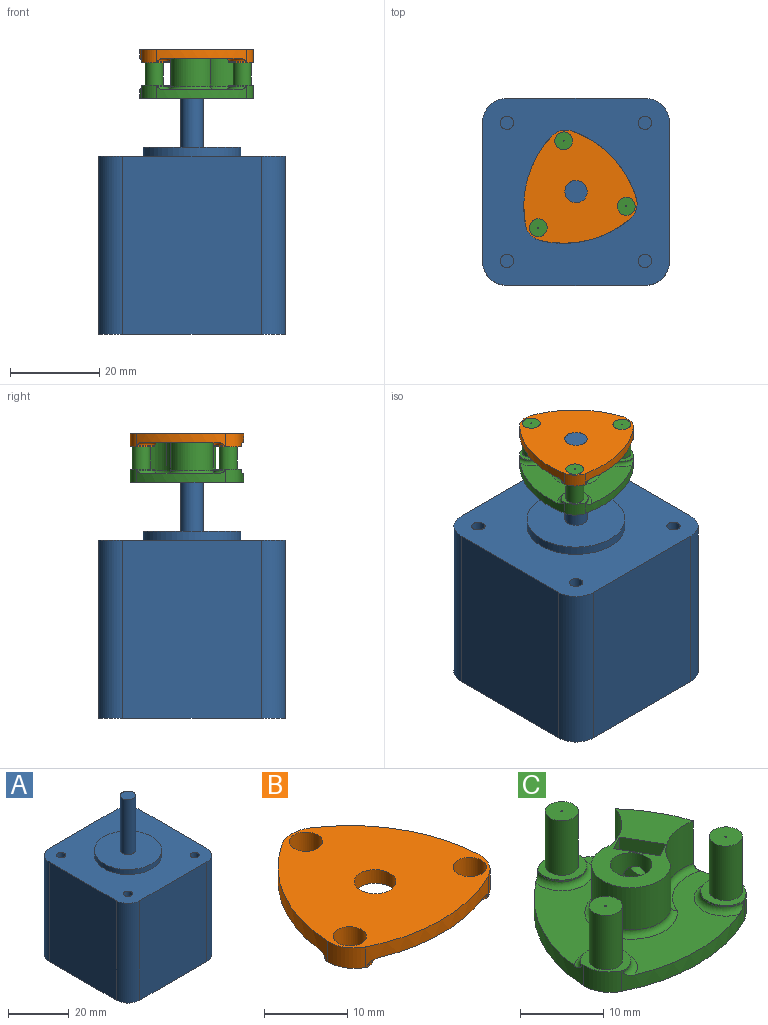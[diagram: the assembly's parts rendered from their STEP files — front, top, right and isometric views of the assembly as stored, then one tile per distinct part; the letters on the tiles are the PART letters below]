
ASSEMBLY  parts=3 mates=2
PART A: 22 faces, bbox 42x42x64 mm
  f0: plane 42x42mm, normal (0,0,1), area 1329.6mm2, adj f1,f2,f3,f4,f5,f6,f7,f8
  f1: plane 40x31mm, normal (1,0,0), area 1240mm2, adj f0,f2,f8,f9
  f2: cylinder r=5.5mm len=40mm, axis (0,0,1), area 345.6mm2, adj f0,f1,f3,f9
  f3: plane 40x31mm, normal (0,1,0), area 1240mm2, adj f0,f2,f4,f9
  f4: cylinder r=5.5mm len=40mm, axis (0,0,1), area 345.6mm2, adj f0,f3,f5,f9
  f5: plane 40x31mm, normal (-1,0,0), area 1240mm2, adj f0,f4,f6,f9
  f6: cylinder r=5.5mm len=40mm, axis (0,0,1), area 345.6mm2, adj f0,f5,f7,f9
  f7: plane 40x31mm, normal (0,-1,0), area 1240mm2, adj f0,f6,f8,f9
  f8: cylinder r=5.5mm len=40mm, axis (0,0,1), area 345.6mm2, adj f0,f1,f7,f9
  f9: plane 42x42mm, normal (0,0,-1), area 1738mm2, adj f1,f2,f3,f4,f5,f6,f7,f8
  f10: cylinder r=11mm len=22mm, axis (0,0,-1), area 138.2mm2, adj f0,f11
  f11: plane 22x22mm, normal (0,0,1), area 360.5mm2, adj f10,f13
  f12: plane 5x5mm, normal (0,0,1), area 19.6mm2, adj f13
  f13: cylinder r=2.5mm len=22mm, axis (0,0,-1), area 345.6mm2, adj f11,f12
  f14: cylinder r=1.5mm len=10mm, axis (0,0,1), area 94.2mm2, adj f0,f15
  f15: plane 3x3mm, normal (0,0,1), area 7.1mm2, adj f14
  f16: cylinder r=1.5mm len=10mm, axis (0,0,1), area 94.2mm2, adj f0,f17
  f17: plane 3x3mm, normal (0,0,1), area 7.1mm2, adj f16
  f18: cylinder r=1.5mm len=10mm, axis (0,0,1), area 94.2mm2, adj f0,f19
  f19: plane 3x3mm, normal (0,0,1), area 7.1mm2, adj f18
  f20: cylinder r=1.5mm len=10mm, axis (0,0,1), area 94.2mm2, adj f0,f21
  f21: plane 3x3mm, normal (0,0,1), area 7.1mm2, adj f20
PART B: 23 faces, bbox 28.5x25.4x3.4 mm
  f0: cylinder r=23mm len=8.94mm, axis (0,0,1), area 19.1mm2, adj f1,f6,f7,f16,f17,f19,f21
  f1: plane 2.6x2mm, normal (0.87,0.5,0), area 6mm2, adj f0,f2,f6,f7
  f2: cylinder r=23mm len=6.57mm, axis (0,0,1), area 19.1mm2, adj f1,f6,f7,f8,f9,f11,f20
  f3: cylinder r=23mm len=18.04mm, axis (0,0,1), area 44.3mm2, adj f6,f7,f8,f9,f11,f12,f13,f15
  f4: cylinder r=23mm len=20.83mm, axis (0,0,1), area 44.3mm2, adj f6,f7,f12,f13,f15,f16,f17,f19
  f5: cylinder r=2.5mm len=5mm, axis (0,0,1), area 31.4mm2, adj f6,f7
  f6: plane 25.28x23.69mm, normal (0,0,-1), area 353.1mm2, adj f0,f1,f2,f3,f4,f5,f20,f21
  f7: plane 25.59x25.35mm, normal (0,0,1), area 423.5mm2, adj f0,f1,f2,f3,f4,f5,f9,f10
  f8: cylinder r=3mm len=6mm, axis (0,0,1), area 2.5mm2, adj f2,f3,f11,f20
  f9: cylinder r=4.35mm len=4.75mm, axis (0,0,1), area 15.1mm2, adj f2,f3,f7,f11
  f10: cylinder r=2mm len=4mm, axis (0,0,1), area 37.7mm2, adj f7,f11
  f11: plane 6x5.35mm, normal (0,0,-1), area 13.2mm2, adj f2,f3,f8,f9,f10
  f12: cylinder r=3mm len=6mm, axis (0,0,1), area 2.5mm2, adj f3,f4,f15,f22
  f13: cylinder r=4.35mm len=4.12mm, axis (0,0,1), area 15.1mm2, adj f3,f4,f7,f15
  f14: cylinder r=2mm len=4mm, axis (0,0,1), area 37.7mm2, adj f7,f15
  f15: plane 6x5.62mm, normal (0,0,-1), area 13.2mm2, adj f3,f4,f12,f13,f14
  f16: cylinder r=3mm len=6mm, axis (0,0,1), area 2.5mm2, adj f0,f4,f19,f21
  f17: cylinder r=4.35mm len=4.12mm, axis (0,0,1), area 15.1mm2, adj f0,f4,f7,f19
  f18: cylinder r=2mm len=4mm, axis (0,0,1), area 37.7mm2, adj f7,f19
  f19: plane 6x5.62mm, normal (0,0,-1), area 13.2mm2, adj f0,f4,f16,f17,f18
  f20: torus R=3.8mm, axis (0,0,1), area 16.1mm2, adj f2,f3,f6,f8
  f21: torus R=3.8mm, axis (0,0,1), area 16.1mm2, adj f0,f4,f6,f16
  f22: torus R=3.8mm, axis (0,0,1), area 16.1mm2, adj f3,f4,f6,f12
PART C: 45 faces, bbox 28.5x25.4x11 mm
  f0: cylinder r=1.6mm len=3.2mm, axis (0.87,0.5,0), area 4.5mm2, adj f11,f37
  f1: plane 2.94x2.6mm, normal (0.87,0.5,0), area 6.6mm2, adj f3,f5,f31,f32
  f2: plane 25.28x23.69mm, normal (0,0,1), area 223.5mm2, adj f3,f5,f7,f9,f39,f40,f41,f42
  f3: cylinder r=23mm len=9mm, axis (0,0,-1), area 43mm2, adj f1,f2,f4,f13,f15,f20,f21,f30
  f4: plane 4.94x2.6mm, normal (0.87,0.5,0), area 12.6mm2, adj f3,f5,f15,f32
  f5: cylinder r=23mm len=9mm, axis (0,0,-1), area 43mm2, adj f1,f2,f4,f6,f15,f16,f17,f28
  f6: cylinder r=4.35mm len=4.75mm, axis (0,0,-1), area 15.1mm2, adj f5,f7,f15,f17
  f7: cylinder r=23mm len=18.04mm, axis (0,0,-1), area 44.3mm2, adj f2,f6,f8,f15,f16,f17,f18,f19
  f8: cylinder r=4.35mm len=4.12mm, axis (0,0,-1), area 15.1mm2, adj f7,f9,f15,f19
  f9: cylinder r=23mm len=20.83mm, axis (0,0,-1), area 44.3mm2, adj f2,f8,f13,f15,f18,f19,f20,f21
  f10: cylinder r=0.1mm len=11mm, axis (0,0,-1), area 6.9mm2, adj f15,f27
  f11: cylinder r=2.5mm len=9mm, axis (0,0,-1), area 132.8mm2, adj f0,f15,f31
  f12: cylinder r=0.1mm len=11mm, axis (0,0,-1), area 6.9mm2, adj f15,f23
  f13: cylinder r=4.35mm len=4.12mm, axis (0,0,-1), area 15.1mm2, adj f3,f9,f15,f21
  f14: cylinder r=0.1mm len=11mm, axis (0,0,-1), area 6.9mm2, adj f15,f25
  f15: plane 25.59x25.35mm, normal (0,0,-1), area 461.2mm2, adj f3,f4,f5,f6,f7,f8,f9,f10
  f16: cylinder r=3mm len=6mm, axis (0,0,-1), area 2.5mm2, adj f5,f7,f17,f44
  f17: plane 6x5.35mm, normal (0,0,1), area 13.2mm2, adj f5,f6,f7,f16,f22
  f18: cylinder r=3mm len=6mm, axis (0,0,-1), area 2.5mm2, adj f7,f9,f19,f43
  f19: plane 6x5.62mm, normal (0,0,1), area 13.2mm2, adj f7,f8,f9,f18,f24
  f20: cylinder r=3mm len=6mm, axis (0,0,-1), area 2.5mm2, adj f3,f9,f21,f42
  f21: plane 6x5.62mm, normal (0,0,1), area 13.2mm2, adj f3,f9,f13,f20,f26
  f22: cylinder r=2mm len=8mm, axis (0,0,-1), area 100.5mm2, adj f17,f23
  f23: plane 4x4mm, normal (0,0,1), area 12.5mm2, adj f12,f22
  f24: cylinder r=2mm len=8mm, axis (0,0,-1), area 100.5mm2, adj f19,f25
  f25: plane 4x4mm, normal (0,0,1), area 12.5mm2, adj f14,f24
  f26: cylinder r=2mm len=8mm, axis (0,0,-1), area 100.5mm2, adj f21,f27
  f27: plane 4x4mm, normal (0,0,1), area 12.5mm2, adj f10,f26
  f28: cylinder r=7.2mm len=6.2mm, axis (0,0,-1), area 49.8mm2, adj f5,f29,f31,f41
  f29: cylinder r=4.75mm len=9.5mm, axis (0,0,-1), area 123.4mm2, adj f28,f30,f31,f40
  f30: cylinder r=7.2mm len=8.25mm, axis (0,0,-1), area 63mm2, adj f3,f29,f31,f39
  f31: plane 16.47x14.32mm, normal (0,0,1), area 83.7mm2, adj f1,f3,f5,f11,f28,f29,f30,f34
  f32: cylinder r=1.6mm len=6.8mm, axis (0.87,0.5,0), area 60.3mm2, adj f1,f3,f4,f5,f38
  f33: plane 3.76x3.62mm, normal (0.25,-0.43,0.87), area 8.4mm2, adj f34,f36,f37,f38
  f34: plane 5.17x2.17mm, normal (0.5,-0.87,0), area 12.9mm2, adj f31,f33,f37,f38
  f35: plane 5.17x2.17mm, normal (-0.5,0.87,0), area 12.9mm2, adj f31,f36,f37,f38
  f36: plane 3.76x3.62mm, normal (-0.25,0.43,0.87), area 8.4mm2, adj f33,f35,f37,f38
  f37: plane 6.85x5.02mm, normal (0.87,0.5,0), area 26.8mm2, adj f0,f31,f33,f34,f35,f36
  f38: plane 6.85x5.02mm, normal (-0.87,-0.5,0), area 26.8mm2, adj f31,f32,f33,f34,f35,f36
  f39: torus R=6.4mm, axis (0,0,1), area 12.7mm2, adj f2,f3,f30,f40
  f40: torus R=5.55mm, axis (0,0,1), area 26.5mm2, adj f2,f29,f39,f41
  f41: torus R=6.4mm, axis (0,0,1), area 9.9mm2, adj f2,f5,f28,f40
  f42: torus R=3.8mm, axis (0,0,1), area 15.9mm2, adj f2,f3,f9,f20
  f43: torus R=3.8mm, axis (0,0,1), area 15.9mm2, adj f2,f7,f9,f18
  f44: torus R=3.8mm, axis (0,0,1), area 15.9mm2, adj f2,f5,f7,f16
PLACE A t=(-0.35,-0.04,8.23)mm fixed
PLACE B rot(axis=(0,0,1),13.7deg) t=(-0.35,-0.04,32.23)mm
PLACE C rot(axis=(0,0,1),13.7deg) t=(-0.35,-0.04,21.23)mm
MATE fastened B.f5 <-> C.f11  axis (0,0,-1) through (-0.35,-0.04,30.23)mm
MATE revolute A.f13 <-> C.f11  axis (0,0,-1) through (-0.35,-0.04,21.23)mm
